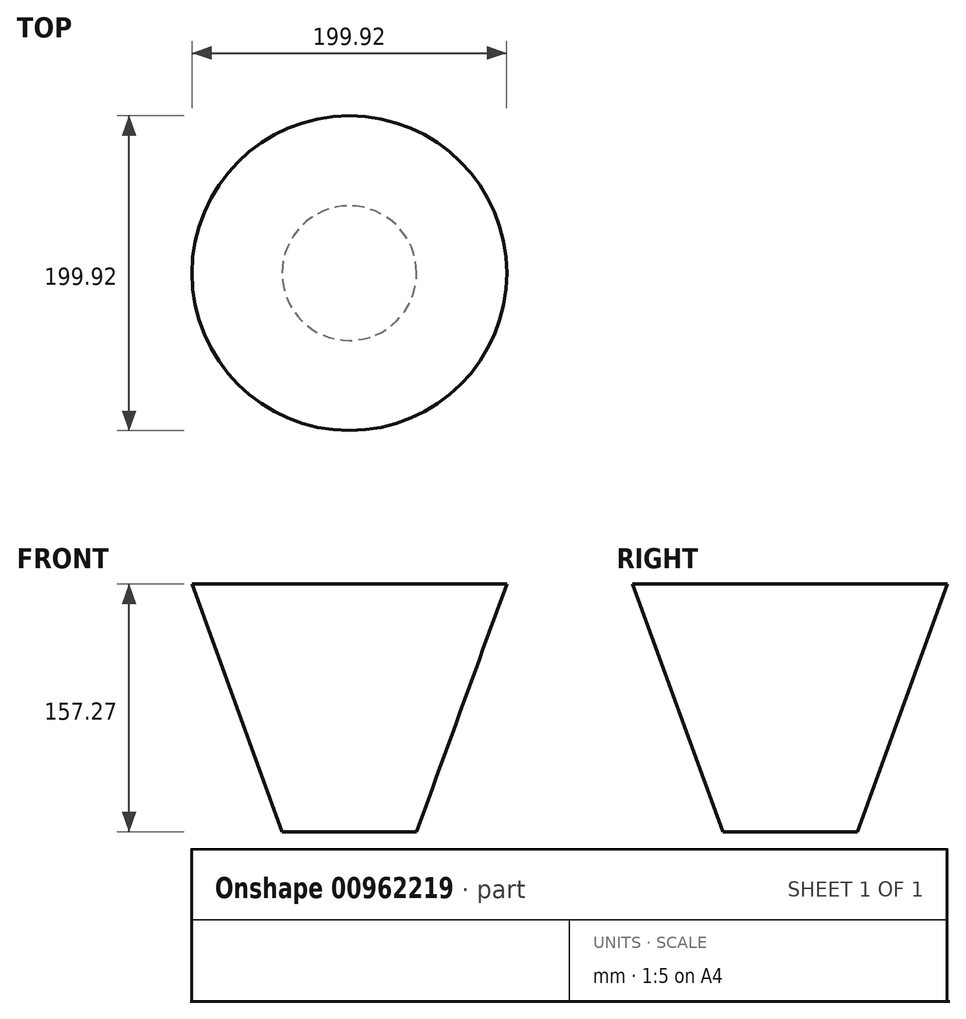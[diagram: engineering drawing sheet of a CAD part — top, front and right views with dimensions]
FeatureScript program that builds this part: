
annotation { "Feature Type Name" : "Feature", "Feature Type Description" : "" }
export const myFeature = defineFeature(function(context is Context, id is Id, definition is map)
    precondition{}
    {
        {
            var Q0;
            Q0=qCreatedBy(makeId("Top.planeOp"),FACE);
            var sketch = newSketch(context, id + "F0", { "sketchPlane" : qUnion([Q0])});
            skCircle(sketch, "E0", {"center": v(0, 0) * mm, "radius": 42.72 * mm});
            skSolve(sketch);
        }
        {
            var Q0;
            Q0=makeQuery(id+"F0.imprint","IMPRINT",FACE,{"disambiguationData":[TD([[makeQuery(id+"F0.imprint","IMPRINT",EDGE,{"derivedFrom":sQuery(id+"F0.wireOp",EDGE,"E0")}),1.0]])]});
            extrude(context, id + "F1", {"entities" : qUnion([Q0]), "depth" : 157.27 * mm, "offsetDistance" : 25.4 * mm, "hasDraft" : true, "draftAngle" : 20 * degree});
        }
    });
